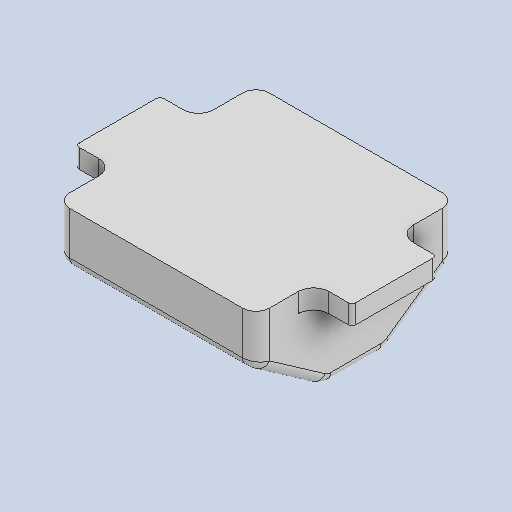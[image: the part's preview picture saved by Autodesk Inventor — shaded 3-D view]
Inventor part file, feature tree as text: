
AUTODESK INVENTOR PART (.ipt)
format: ipt  version: 2022 (Build 260153000, 153)  size: 255,488 bytes
history: native  units: mm
features: other x4, extrude x3, sketch x3, projected_geometry x3, fillet x2, reference x2
ambient origin geometry x8: Origin, YZ Plane, XZ Plane, XY Plane, X Axis, Y Axis, Z Axis, Center Point
bodies: Body1 (feature_tree)
feature tree (17):
  other  "Твердое тело1"
  extrude  "Выдавливание1"  Depth=0.3mm
  extrude  "Выдавливание2"  Depth=0.3mm
  extrude  "Выдавливание3"  Depth=1.0mm TaperAngle=0.0deg
  fillet  "Сопряжение2"  Radius=4.0mm
  fillet  "Сопряжение3"  Radius=2.5mm
  sketch  "Эскиз1"
  reference  "Ссылка1"
  reference  "Ссылка2"
  sketch  "Эскиз2"
  projected_geometry  "Спроецированная петля1"
  sketch  "Эскиз3"
  projected_geometry  "Спроецированная петля2"
  projected_geometry  "Спроецированная петля4"
  other  "<userpath>\Documents\Git\MZCAT_2024\MZCAT_4.iam"
  other  "MZCAT_4.iam"
  other  "magazine_spring:1"
